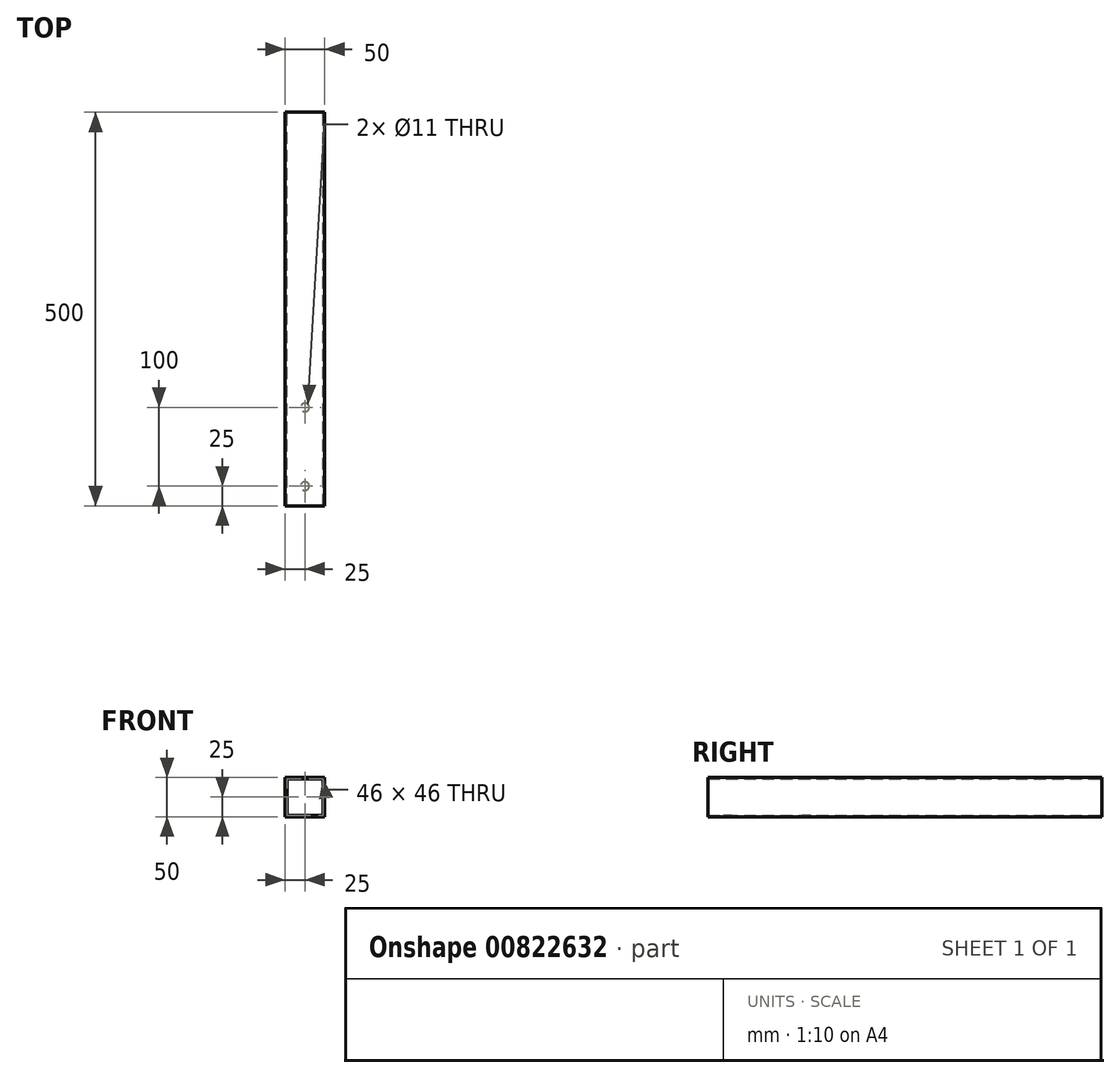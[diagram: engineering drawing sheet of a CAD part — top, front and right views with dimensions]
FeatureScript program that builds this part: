
annotation { "Feature Type Name" : "Feature", "Feature Type Description" : "" }
export const myFeature = defineFeature(function(context is Context, id is Id, definition is map)
    precondition{}
    {
        {
            var Q0;
            Q0=qCreatedBy(makeId("Front.planeOp"),FACE);
            var sketch = newSketch(context, id + "F0", { "sketchPlane" : qUnion([Q0])});
            skLineSegment(sketch, "E0.bottom", {"start": v(-25, 25) * mm, "end": v(25, 25) * mm});
            skLineSegment(sketch, "E0.top", {"start": v(-25, -25) * mm, "end": v(25, -25) * mm});
            skLineSegment(sketch, "E0.left", {"start": v(-25, 25) * mm, "end": v(-25, -25) * mm});
            skLineSegment(sketch, "E0.right", {"start": v(25, 25) * mm, "end": v(25, -25) * mm});
            skPoint(sketch, "E0.middle", {"position": v(0, 0) * mm});
            skLineSegment(sketch, "E1.0", {"start": v(-23, 23) * mm, "end": v(23, 23) * mm});
            skLineSegment(sketch, "E1.1", {"start": v(-23, 23) * mm, "end": v(-23, -23) * mm});
            skLineSegment(sketch, "E1.2", {"start": v(-23, -23) * mm, "end": v(23, -23) * mm});
            skLineSegment(sketch, "E1.3", {"start": v(23, 23) * mm, "end": v(23, -23) * mm});
            skSolve(sketch);
        }
        {
            var Q0;
            Q0=makeQuery(id+"F0.imprint","IMPRINT",FACE,{"disambiguationData":[TD([[makeQuery(id+"F0.imprint","IMPRINT",EDGE,{"derivedFrom":sQuery(id+"F0.wireOp",EDGE,"E0.bottom")}),-1.0]])]});
            extrude(context, id + "F1", {"entities" : qUnion([Q0]), "depth" : 500 * mm, "offsetDistance" : 25 * mm, "symmetric" : true});
        }
        {
            var Q0;
            Q0=makeQuery(id+"F1.opExtrude","SWEPT_FACE",FACE,{"disambiguationData":[OSD([sQuery(id+"F0.wireOp",EDGE,"E0.top")])]});
            var sketch = newSketch(context, id + "F2", { "sketchPlane" : qUnion([Q0])});
            skLineSegment(sketch, "E2", {"start": v(0, 250) * mm, "end": v(0, 225) * mm});
            skLineSegment(sketch, "E3", {"start": v(0, 225) * mm, "end": v(0, 125) * mm});
            skSolve(sketch);
        }
        {
            var Q0;
            Q0=sQuery(id+"F2.wireOp",VERTEX,"E2.end");
            var Q1;
            Q1=sQuery(id+"F2.wireOp",VERTEX,"E3.end");
            var Q2;
            Q2=makeQuery(id+"F1.opExtrude","SWEPT_BODY",BODY,{"disambiguationData":[OSD([sQuery(id+"F0.wireOp",EDGE,"E0.bottom"),sQuery(id+"F0.wireOp",EDGE,"E0.top"),sQuery(id+"F0.wireOp",EDGE,"E0.left"),sQuery(id+"F0.wireOp",EDGE,"E0.right"),sQuery(id+"F0.wireOp",EDGE,"E1.0"),sQuery(id+"F0.wireOp",EDGE,"E1.1"),sQuery(id+"F0.wireOp",EDGE,"E1.2"),sQuery(id+"F0.wireOp",EDGE,"E1.3")])]});
            hole(context, id + "F3", {"style" : HoleStyle.SIMPLE, "endStyle" : HoleEndStyle.BLIND, "holeDiameter" : 11 * mm, "majorDiameter" : 5 * mm, "holeDepth" : 2 * mm, "isTappedThrough" : true, "tappedDepth" : 12 * mm, "tapClearance" : 3, "locations" : qUnion([Q0, Q1]), "scope" : qUnion([Q2])});
        }
    });
